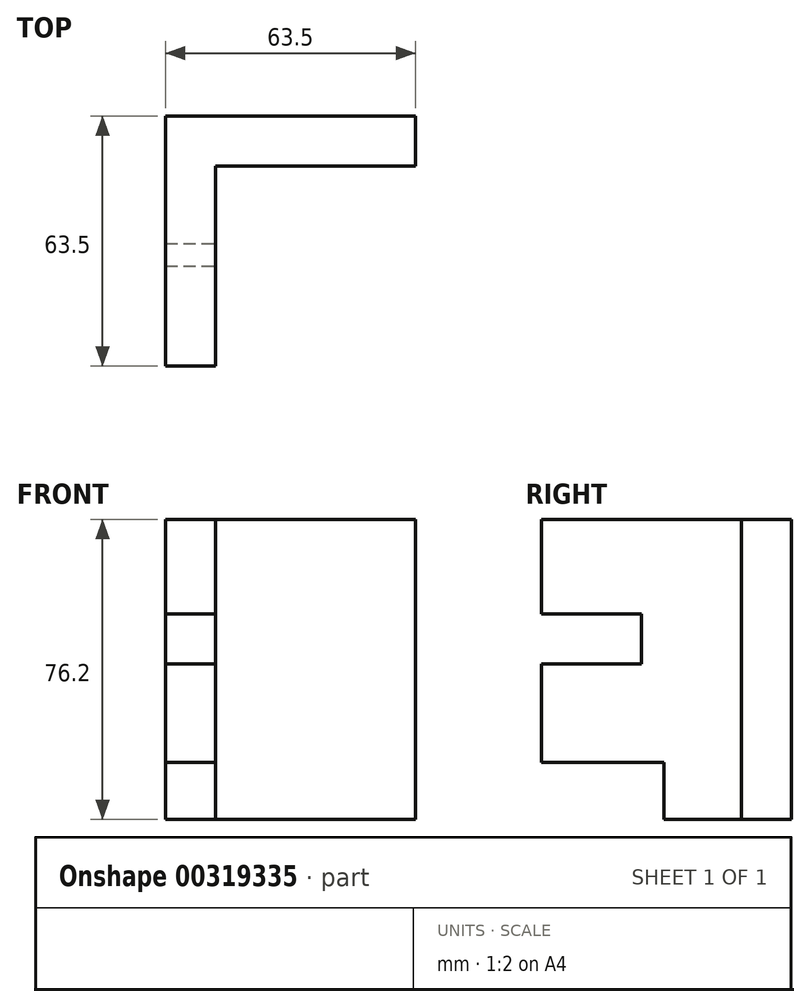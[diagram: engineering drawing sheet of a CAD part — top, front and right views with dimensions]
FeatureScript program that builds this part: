
annotation { "Feature Type Name" : "Feature", "Feature Type Description" : "" }
export const myFeature = defineFeature(function(context is Context, id is Id, definition is map)
    precondition{}
    {
        {
            var Q0;
            Q0=qCreatedBy(makeId("Top.planeOp"),FACE);
            var sketch = newSketch(context, id + "F0", { "sketchPlane" : qUnion([Q0])});
            skLineSegment(sketch, "E0", {"start": v(-39.3, -41.81) * mm, "end": v(-39.3, 21.69) * mm});
            skLineSegment(sketch, "E1", {"start": v(-39.3, 21.69) * mm, "end": v(24.2, 21.69) * mm});
            skLineSegment(sketch, "E2", {"start": v(24.2, 21.69) * mm, "end": v(24.2, 8.99) * mm});
            skLineSegment(sketch, "E3", {"start": v(24.2, 8.99) * mm, "end": v(-26.6, 8.99) * mm});
            skLineSegment(sketch, "E4", {"start": v(-26.6, 8.99) * mm, "end": v(-26.6, -41.81) * mm});
            skLineSegment(sketch, "E5", {"start": v(-26.6, -41.81) * mm, "end": v(-39.3, -41.81) * mm});
            skSolve(sketch);
        }
        {
            var Q0;
            Q0 = qSketchRegion(id + "F0", true);
            extrude(context, id + "F1", {"entities" : qUnion([Q0]), "depth" : 76.2 * mm});
        }
        {
            var Q0;
            Q0=makeQuery(id+"F1.opExtrude","SWEPT_FACE",FACE,{"disambiguationData":[OSD([sQuery(id+"F0.wireOp",EDGE,"E4")])]});
            var sketch = newSketch(context, id + "F2", { "sketchPlane" : qUnion([Q0])});
            skLineSegment(sketch, "E6", {"start": v(-41.81, 14.45) * mm, "end": v(-10.68, 14.45) * mm});
            skLineSegment(sketch, "E7", {"start": v(-10.68, 14.45) * mm, "end": v(-10.68, 0) * mm});
            skLineSegment(sketch, "E8", {"start": v(-10.68, 0) * mm, "end": v(-41.81, 0) * mm});
            skLineSegment(sketch, "E9", {"start": v(-41.81, 0) * mm, "end": v(-41.81, 14.45) * mm});
            skSolve(sketch);
        }
        {
            var Q0;
            Q0 = qSketchRegion(id + "F2", true);
            extrude(context, id + "F3", {"entities" : qUnion([Q0]), "operationType" : NewBodyOperationType.REMOVE, "oppositeDirection" : true, "depth" : 25.4 * mm});
        }
        {
            var Q0;
            Q0=makeQuery(id+"F1.opExtrude","SWEPT_FACE",FACE,{"disambiguationData":[OSD([sQuery(id+"F0.wireOp",EDGE,"E4")])]});
            var sketch = newSketch(context, id + "F4", { "sketchPlane" : qUnion([Q0])});
            skLineSegment(sketch, "E10", {"start": v(-41.81, 52.16) * mm, "end": v(-16.41, 52.16) * mm});
            skLineSegment(sketch, "E11", {"start": v(-16.41, 52.16) * mm, "end": v(-16.41, 39.46) * mm});
            skLineSegment(sketch, "E12", {"start": v(-16.41, 39.46) * mm, "end": v(-41.81, 39.46) * mm});
            skLineSegment(sketch, "E13", {"start": v(-41.81, 39.46) * mm, "end": v(-41.81, 52.16) * mm});
            skSolve(sketch);
        }
        {
            var Q0;
            Q0 = qSketchRegion(id + "F4", true);
            extrude(context, id + "F5", {"entities" : qUnion([Q0]), "operationType" : NewBodyOperationType.REMOVE, "oppositeDirection" : true, "depth" : 25.4 * mm});
        }
    });
